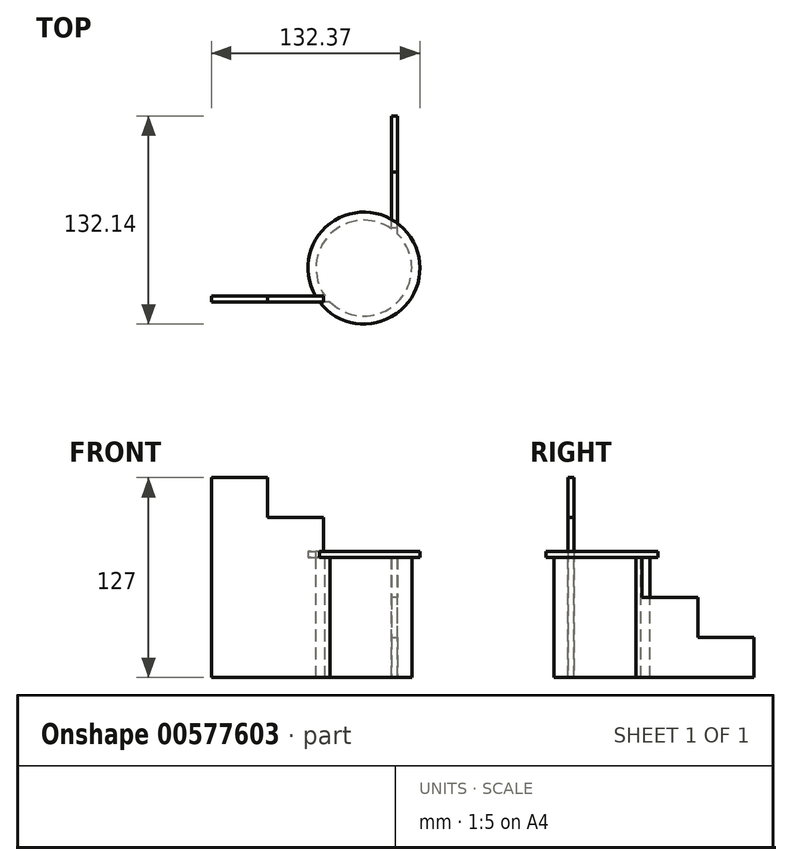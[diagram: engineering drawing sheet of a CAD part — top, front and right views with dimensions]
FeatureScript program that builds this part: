
annotation { "Feature Type Name" : "Feature", "Feature Type Description" : "" }
export const myFeature = defineFeature(function(context is Context, id is Id, definition is map)
    precondition{}
    {
        {
            var Q0;
            Q0=qCreatedBy(makeId("Top.planeOp"),FACE);
            var sketch = newSketch(context, id + "F0", { "sketchPlane" : qUnion([Q0])});
            skLineSegment(sketch, "E0.bottom", {"start": v(57.14, -57.15) * mm, "end": v(-57.16, -57.15) * mm});
            skLineSegment(sketch, "E0.top", {"start": v(57.14, -60.96) * mm, "end": v(-57.16, -60.96) * mm});
            skLineSegment(sketch, "E0.left", {"start": v(57.14, -57.15) * mm, "end": v(57.14, -60.96) * mm});
            skLineSegment(sketch, "E0.right", {"start": v(-57.16, -57.15) * mm, "end": v(-57.16, -60.96) * mm});
            skLineSegment(sketch, "E1.bottom", {"start": v(57.14, -60.96) * mm, "end": v(60.95, -60.96) * mm});
            skLineSegment(sketch, "E1.top", {"start": v(57.14, 57.15) * mm, "end": v(60.95, 57.15) * mm});
            skLineSegment(sketch, "E1.left", {"start": v(57.14, -60.96) * mm, "end": v(57.14, 57.15) * mm});
            skLineSegment(sketch, "E1.right", {"start": v(60.95, -60.96) * mm, "end": v(60.95, 57.15) * mm});
            skSolve(sketch);
        }
        {
            var Q0;
            Q0=qSketchRegion(id+"F0",true);
            extrude(context, id + "F1", {"entities" : qUnion([Q0]), "depth" : 127 * mm, "offsetDistance" : 25.4 * mm});
        }
        {
            var Q0;
            Q0=makeQuery(id+"F1.opExtrude","CAP_FACE",FACE,{"disambiguationData":[OSD([sQuery(id+"F0.wireOp",EDGE,"E0.bottom"),sQuery(id+"F0.wireOp",EDGE,"E0.top"),sQuery(id+"F0.wireOp",EDGE,"E0.right"),sQuery(id+"F0.wireOp",EDGE,"E1.bottom"),sQuery(id+"F0.wireOp",EDGE,"E1.top"),sQuery(id+"F0.wireOp",EDGE,"E1.left"),sQuery(id+"F0.wireOp",EDGE,"E1.right")])],"isStart":false});
            var sketch = newSketch(context, id + "F2", { "sketchPlane" : qUnion([Q0])});
            skLineSegment(sketch, "E2.bottom", {"start": v(-57.16, -60.96) * mm, "end": v(-21.56, -60.96) * mm});
            skLineSegment(sketch, "E2.top", {"start": v(-57.16, -57.15) * mm, "end": v(-21.56, -57.15) * mm});
            skLineSegment(sketch, "E2.left", {"start": v(-57.16, -60.96) * mm, "end": v(-57.16, -57.15) * mm});
            skLineSegment(sketch, "E2.right", {"start": v(-21.56, -60.96) * mm, "end": v(-21.56, -57.15) * mm});
            skSolve(sketch);
        }
        {
            var Q0;
            {var subQ2=sQuery(id+"F2.wireOp",EDGE,"E2.right");Q0=makeQuery(id+"F2.imprint","IMPRINT",FACE,{"disambiguationData":[TD([[makeQuery(id+"F2.imprint","IMPRINT",EDGE,{"derivedFrom":subQ2}),-1.0]])]});}
            var sketch = newSketch(context, id + "F3", { "sketchPlane" : qUnion([Q0])});
            skLineSegment(sketch, "E3.bottom", {"start": v(-21.56, -60.96) * mm, "end": v(13.98, -60.96) * mm});
            skLineSegment(sketch, "E3.top", {"start": v(-21.56, -57.15) * mm, "end": v(13.98, -57.15) * mm});
            skLineSegment(sketch, "E3.left", {"start": v(-21.56, -60.96) * mm, "end": v(-21.56, -57.15) * mm});
            skLineSegment(sketch, "E3.right", {"start": v(13.98, -60.96) * mm, "end": v(13.98, -57.15) * mm});
            skSolve(sketch);
        }
        {
            var Q0;
            {var subQ2=sQuery(id+"F2.wireOp",EDGE,"E2.right");Q0=makeQuery(id+"F2.imprint","IMPRINT",FACE,{"disambiguationData":[TD([[makeQuery(id+"F2.imprint","IMPRINT",EDGE,{"derivedFrom":subQ2}),-1.0]])]});}
            var sketch = newSketch(context, id + "F4", { "sketchPlane" : qUnion([Q0])});
            skLineSegment(sketch, "E4.bottom", {"start": v(60.94, 57.16) * mm, "end": v(57.04, 57.16) * mm});
            skLineSegment(sketch, "E4.top", {"start": v(60.94, 21.5) * mm, "end": v(57.04, 21.5) * mm});
            skLineSegment(sketch, "E4.left", {"start": v(60.94, 57.16) * mm, "end": v(60.94, 21.5) * mm});
            skLineSegment(sketch, "E4.right", {"start": v(57.04, 57.16) * mm, "end": v(57.04, 21.5) * mm});
            skSolve(sketch);
        }
        {
            var Q0;
            {var subQ2=sQuery(id+"F2.wireOp",EDGE,"E2.right");Q0=makeQuery(id+"F2.imprint","IMPRINT",FACE,{"disambiguationData":[TD([[makeQuery(id+"F2.imprint","IMPRINT",EDGE,{"derivedFrom":subQ2}),-1.0]])]});}
            var sketch = newSketch(context, id + "F5", { "sketchPlane" : qUnion([Q0])});
            skLineSegment(sketch, "E5.bottom", {"start": v(61.03, 21.57) * mm, "end": v(56.87, 21.57) * mm});
            skLineSegment(sketch, "E5.top", {"start": v(61.03, -14) * mm, "end": v(56.87, -14) * mm});
            skLineSegment(sketch, "E5.left", {"start": v(61.03, 21.57) * mm, "end": v(61.03, -14) * mm});
            skLineSegment(sketch, "E5.right", {"start": v(56.87, 21.57) * mm, "end": v(56.87, -14) * mm});
            skSolve(sketch);
        }
        {
            var Q0;
            Q0=qSketchRegion(id+"F3",true);
            extrude(context, id + "F6", {"entities" : qUnion([Q0]), "operationType" : NewBodyOperationType.REMOVE, "oppositeDirection" : true, "depth" : 25.4 * mm, "offsetDistance" : 25.4 * mm});
        }
        {
            var Q0;
            Q0=qSketchRegion(id+"F5",true);
            extrude(context, id + "F7", {"entities" : qUnion([Q0]), "operationType" : NewBodyOperationType.REMOVE, "oppositeDirection" : true, "depth" : 76.2 * mm, "offsetDistance" : 25.4 * mm});
        }
        {
            var Q0;
            {var subQ2=sQuery(id+"F2.wireOp",EDGE,"E2.right");Q0=makeQuery(id+"F2.imprint","IMPRINT",FACE,{"disambiguationData":[TD([[makeQuery(id+"F2.imprint","IMPRINT",EDGE,{"derivedFrom":subQ2}),-1.0]])]});}
            var sketch = newSketch(context, id + "F8", { "sketchPlane" : qUnion([Q0])});
            skLineSegment(sketch, "E6.bottom", {"start": v(13.92, -61.53) * mm, "end": v(78.38, -61.53) * mm});
            skLineSegment(sketch, "E6.top", {"start": v(13.92, -13.89) * mm, "end": v(78.38, -13.89) * mm});
            skLineSegment(sketch, "E6.left", {"start": v(13.92, -61.53) * mm, "end": v(13.92, -13.89) * mm});
            skLineSegment(sketch, "E6.right", {"start": v(78.38, -61.53) * mm, "end": v(78.38, -13.89) * mm});
            skSolve(sketch);
        }
        {
            var Q0;
            Q0=qSketchRegion(id+"F8",true);
            extrude(context, id + "F9", {"entities" : qUnion([Q0]), "operationType" : NewBodyOperationType.REMOVE, "oppositeDirection" : true, "depth" : 50.8 * mm, "offsetDistance" : 25.4 * mm});
        }
        {
            var Q0;
            Q0=makeQuery(id+"F9.boolean.opBoolean","COPY",FACE,{"derivedFrom":makeQuery(id+"F9.opExtrude","CAP_FACE",FACE,{"disambiguationData":[OSD([sQuery(id+"F8.wireOp",EDGE,"E6.bottom"),sQuery(id+"F8.wireOp",EDGE,"E6.top"),sQuery(id+"F8.wireOp",EDGE,"E6.left"),sQuery(id+"F8.wireOp",EDGE,"E6.right")])],"isStart":false})});
            var sketch = newSketch(context, id + "F10", { "sketchPlane" : qUnion([Q0])});
            skCircle(sketch, "E7", {"center": v(39.65, -39.43) * mm, "radius": 35.56 * mm});
            skSolve(sketch);
        }
        {
            var Q0;
            Q0=qSketchRegion(id+"F10",true);
            extrude(context, id + "F11", {"entities" : qUnion([Q0]), "operationType" : NewBodyOperationType.ADD, "depth" : 3.8 * mm, "offsetDistance" : 25.4 * mm});
        }
        {
            var Q0;
            Q0=qSketchRegion(id+"F4",true);
            extrude(context, id + "F12", {"entities" : qUnion([Q0]), "operationType" : NewBodyOperationType.REMOVE, "oppositeDirection" : true, "depth" : 101.6 * mm, "offsetDistance" : 25.4 * mm});
        }
        {
            var Q0;
            Q0=makeQuery(id+"F11.opExtrude","CAP_FACE",FACE,{"disambiguationData":[OSD([sQuery(id+"F10.wireOp",EDGE,"E7")])],"isStart":true});
            var sketch = newSketch(context, id + "F13", { "sketchPlane" : qUnion([Q0])});
            skCircle(sketch, "E8", {"center": v(39.65, 39.43) * mm, "radius": 30.4 * mm});
            skSolve(sketch);
        }
        {
            var Q0;
            Q0 = qSketchRegion(id + "F13", true);
            extrude(context, id + "F14", {"entities" : qUnion([Q0]), "operationType" : NewBodyOperationType.ADD, "depth" : 76.2 * mm, "offsetDistance" : 25.4 * mm});
        }
    });
